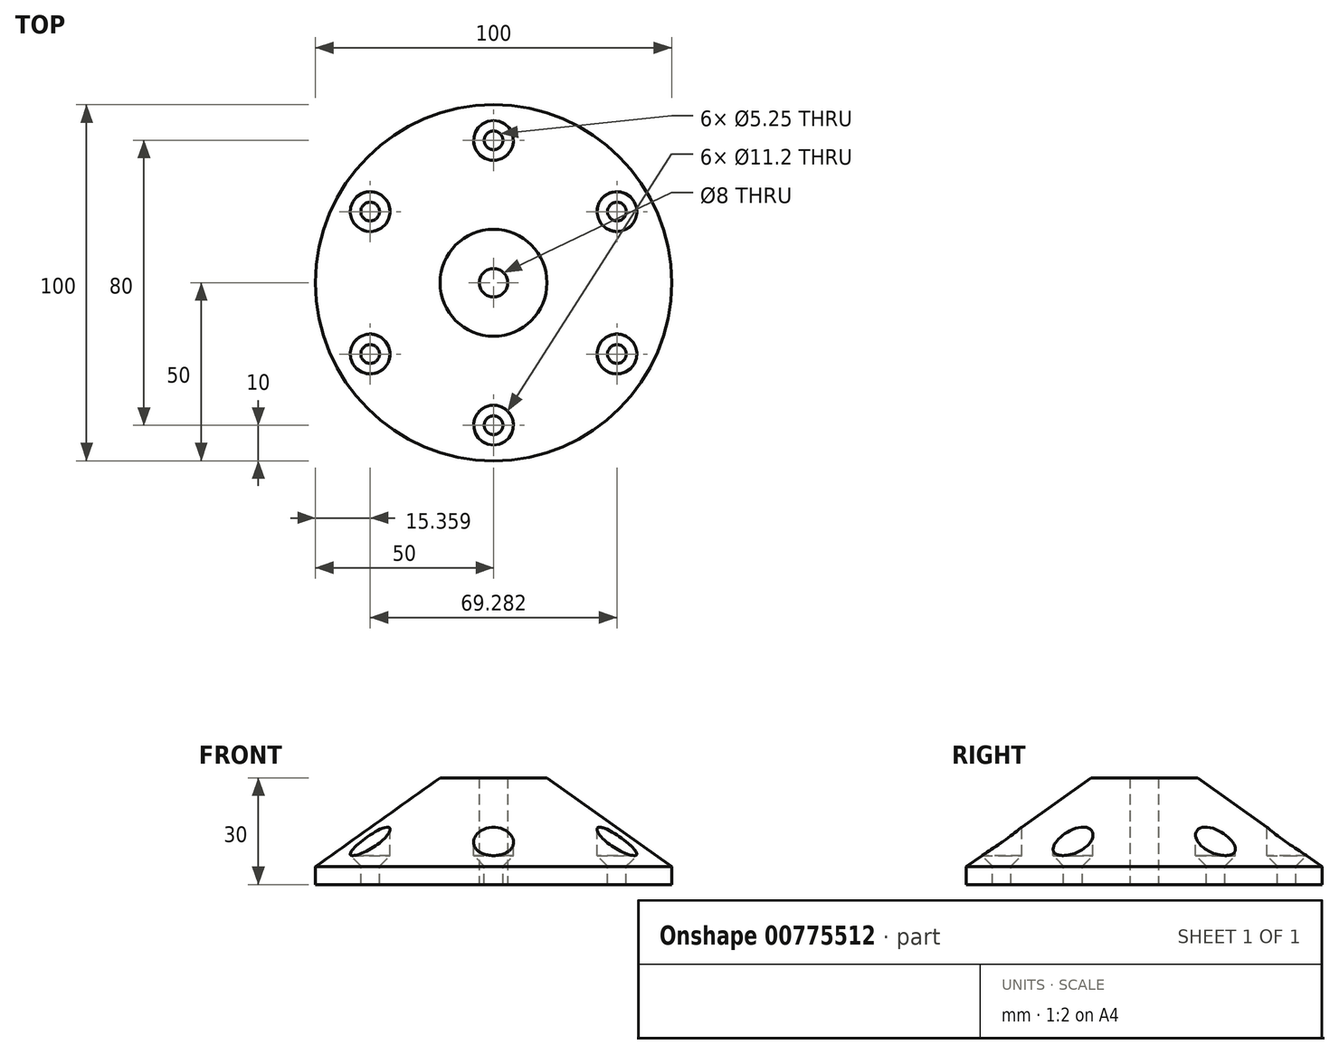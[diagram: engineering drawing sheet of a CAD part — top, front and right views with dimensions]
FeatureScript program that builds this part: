
annotation { "Feature Type Name" : "Feature", "Feature Type Description" : "" }
export const myFeature = defineFeature(function(context is Context, id is Id, definition is map)
    precondition{}
    {
        {
            var Q0;
            Q0=qCreatedBy(makeId("Front.planeOp"),FACE);
            var sketch = newSketch(context, id + "F0", { "sketchPlane" : qUnion([Q0])});
            skLineSegment(sketch, "E0", {"start": v(0, 0) * mm, "end": v(0, 32.62) * mm, "construction": true});
            skLineSegment(sketch, "E1", {"start": v(-4, 0) * mm, "end": v(-4, 30) * mm});
            skLineSegment(sketch, "E2", {"start": v(-4, 0) * mm, "end": v(-50, 0) * mm});
            skLineSegment(sketch, "E3", {"start": v(-15, 30) * mm, "end": v(-4, 30) * mm});
            skLineSegment(sketch, "E4", {"start": v(-50, 0) * mm, "end": v(-50, 5) * mm});
            skLineSegment(sketch, "E5", {"start": v(-50, 5) * mm, "end": v(-15, 30) * mm});
            skSolve(sketch);
        }
        {
            var Q0;
            Q0=qSketchRegion(id+"F0",true);
            var Q1;
            Q1=sQuery(id+"F0.wireOp",EDGE,"E0");
            revolve(context, id + "F1", {"surfaceOperationType" : NewSurfaceOperationType.NEW, "entities" : qUnion([Q0]), "axis" : qUnion([Q1]), "revolveType" : RevolveType.FULL});
        }
        {
            var Q0;
            Q0=makeQuery(id+"F1.opRevolve","SWEPT_FACE",FACE,{"disambiguationData":[OSD([sQuery(id+"F0.wireOp",EDGE,"E3")])]});
            var sketch = newSketch(context, id + "F2", { "sketchPlane" : qUnion([Q0])});
            skCircle(sketch, "E6", {"center": v(0, 0) * mm, "radius": 40 * mm, "construction": true});
            skPoint(sketch, "E7", {"position": v(0, 40) * mm});
            skPoint(sketch, "E8.1.0", {"position": v(-34.64, 20) * mm});
            skPoint(sketch, "E8.2.0", {"position": v(-34.64, -20) * mm});
            skPoint(sketch, "E8.3.0", {"position": v(0, -40) * mm});
            skPoint(sketch, "E8.4.0", {"position": v(34.64, -20) * mm});
            skPoint(sketch, "E8.5.0", {"position": v(34.64, 20) * mm});
            skSolve(sketch);
        }
        {
            var Q0;
            Q0=sQuery(id+"F2.wireOp",VERTEX,"E7");
            var Q1;
            Q1=sQuery(id+"F2.wireOp",VERTEX,"E8.5.0");
            var Q2;
            Q2=sQuery(id+"F2.wireOp",VERTEX,"E8.4.0");
            var Q3;
            Q3=sQuery(id+"F2.wireOp",VERTEX,"E8.3.0");
            var Q4;
            Q4=sQuery(id+"F2.wireOp",VERTEX,"E8.2.0");
            var Q5;
            Q5=sQuery(id+"F2.wireOp",VERTEX,"E8.1.0");
            var Q6;
            Q6=makeQuery(id+"F1.opRevolve","SWEPT_BODY",BODY,{"disambiguationData":[OSD([sQuery(id+"F0.wireOp",EDGE,"E1"),sQuery(id+"F0.wireOp",EDGE,"E2"),sQuery(id+"F0.wireOp",EDGE,"E3"),sQuery(id+"F0.wireOp",EDGE,"E4"),sQuery(id+"F0.wireOp",EDGE,"E5")])]});
            hole(context, id + "F3", {"style" : HoleStyle.C_SINK, "endStyle" : HoleEndStyle.THROUGH, "standardTappedOrClearance" : lookupTablePath({ "standard" : "ISO", "fit" : "Close", "size" : "M5", "type" : "Clearance" }), "standardBlindInLast" : lookupTablePath({ "fit" : "Close", "standard" : "ISO", "size" : "M5", "type" : "Clearance" }), "holeDiameter" : 5.25 * mm, "cSinkDiameter" : 11.2 * mm, "cSinkAngle" : 90 * degree, "majorDiameter" : 5 * mm, "isTappedThrough" : true, "tappedDepth" : 12 * mm, "tapClearance" : 3, "locations" : qUnion([Q0, Q1, Q2, Q3, Q4, Q5]), "scope" : qUnion([Q6])});
        }
    });
